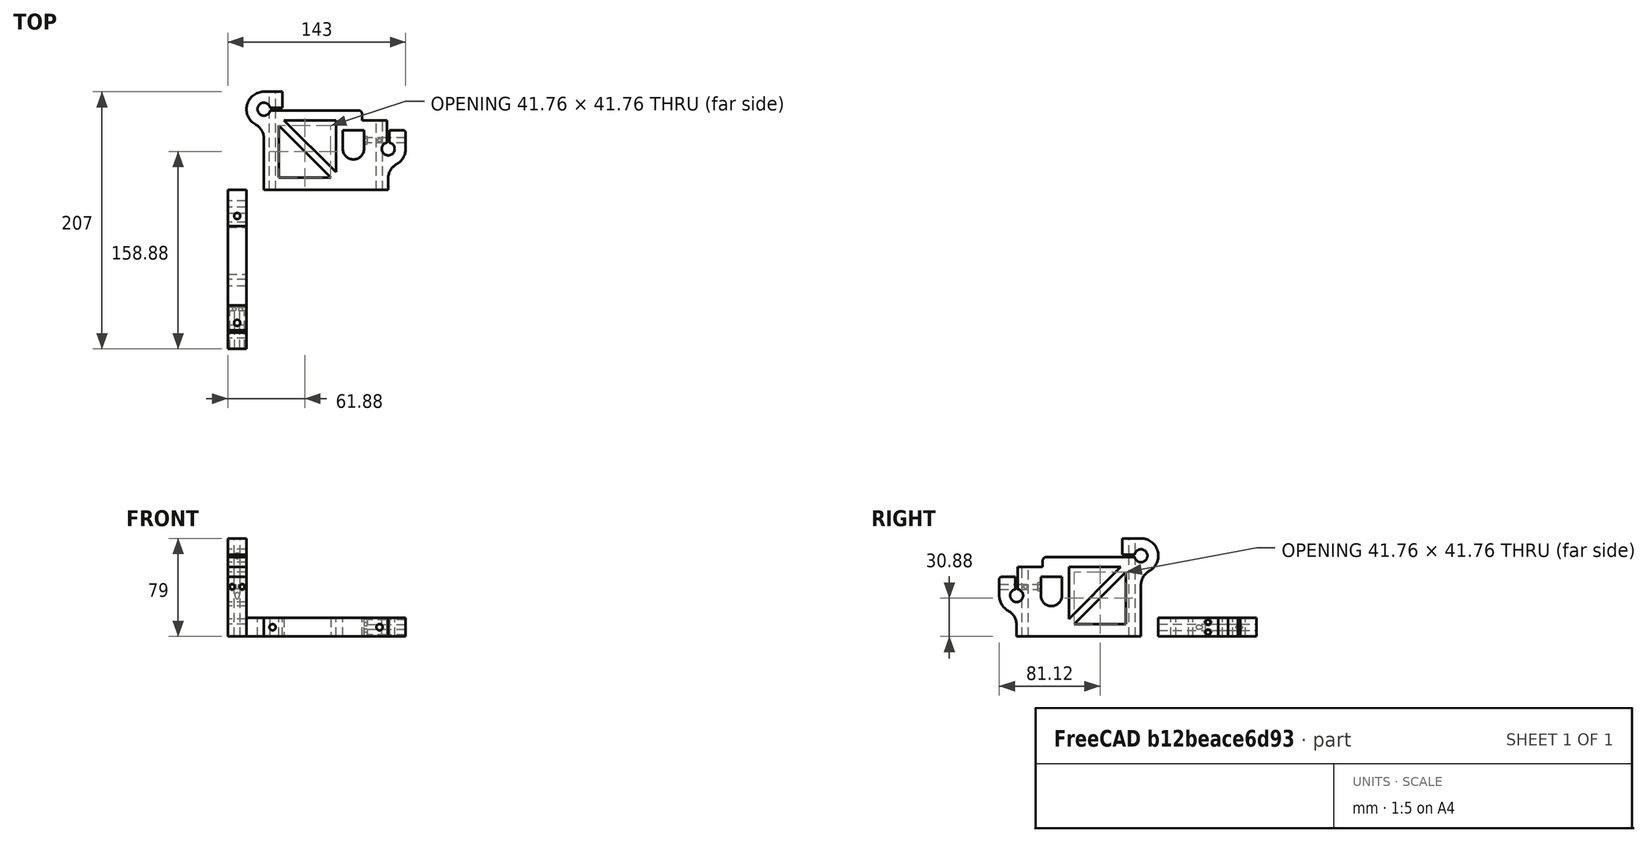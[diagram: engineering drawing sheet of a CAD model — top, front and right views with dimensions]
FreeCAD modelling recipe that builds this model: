
FCSTD DOCUMENT  (FreeCAD 0.15R4666 (Git))
Label: x_right_holder_A
License: All rights reserved
LicenseURL: http://en.wikipedia.org/wiki/All_rights_reserved
objects: Part::Box×9, Part::Cylinder×9, Part::MultiFuse×8, Part::Cut×7, Part::Fillet×3, Part::Prism×2, Part::Feature×2, Mesh::Feature×1
note: 40 computed .brp shape members not serialized (recipe doc carries the construction recipe); baked Part::Feature solids carry a one-line shape summary decoded from their .brp

FEATURE [Part::Box] Box  label="Cubo"
  Height = 15
  Length = 100
  Placement = pos=(14,0,0) rot=(0,0,1;0rad)
  Width = 56
FEATURE [Part::Box] Box001  label="Cubo001"
  Height = 15
  Length = 15
  Placement = pos=(14,56,0) rot=(0,0,1;0rad)
  Width = 23
FEATURE [Part::Box] Box002  label="Cubo002"
  Height = 15
  Length = 64
  Placement = pos=(29,56,0) rot=(0,0,1;0rad)
  Width = 8
FEATURE [Part::Box] Box003  label="Cubo003"
  Height = 15
  Length = 14
  Placement = pos=(114,33,0) rot=(0,0,1;0rad)
  Width = 15
FEATURE [Part::Cylinder] Cylinder  label="Cilindro"
  Angle = 360
  Height = 15
  Placement = pos=(14,65,0) rot=(0,0,1;0rad)
  Radius = 14
FEATURE [Part::Cylinder] Cylinder001  label="Cilindro001"
  Angle = 360
  Height = 15
  Placement = pos=(114,33,0) rot=(0,0,1;0rad)
  Radius = 14
FEATURE [Part::MultiFuse] Fusion
  Shapes = -> [Box,Cylinder001,Cylinder,Box003,Box002,Box001]
FEATURE [Part::Box] Box004  label="Cubo004"
  Height = 15
  Length = 46
  Placement = pos=(26,10,0) rot=(0,0,1;0rad)
  Width = 46
FEATURE [Part::Cut] Cut
  Base = -> Fusion
  Tool = -> Box004
FEATURE [Part::Fillet] Fillet
  Base = -> Cut
  Edges = 2 edges r=13: [Edge60,Edge63]
FEATURE [Part::Fillet] Fillet001
  Base = -> Fillet
  Edges = 1 edges r=3: [Edge76]
FEATURE [Part::Fillet] Fillet002  label="body"
  Base = -> Fillet001
  Edges = 1 edges r=2: [Edge89]
FEATURE [Part::Cylinder] Cylinder002  label="Cilindro002"
  Angle = 360
  Height = 17
  Placement = pos=(14,65,-1) rot=(0,0,1;0rad)
  Radius = 5.2
FEATURE [Part::Cylinder] Cylinder003  label="Cilindro003"
  Angle = 360
  Height = 17
  Placement = pos=(114,33,-1) rot=(0,0,1;0rad)
  Radius = 5.2
FEATURE [Part::MultiFuse] Fusion001  label="rod_holes"
  Shapes = -> [Cylinder002,Cylinder003]
FEATURE [Part::Box] Box006  label="Cubo006"
  Height = 15
  Length = 17
  Placement = pos=(77.5,33,0) rot=(0,0,1;0rad)
  Width = 15
FEATURE [Part::Cylinder] Cylinder004  label="Cilindro004"
  Angle = 360
  Height = 15
  Placement = pos=(86,33,0) rot=(0,0,1;0rad)
  Radius = 8.5
FEATURE [Part::MultiFuse] Fusion002  label="threaded_rod_hole"
  Shapes = -> [Box006,Cylinder004]
FEATURE [Part::Box] Box007  label="Cubo007"
  Height = 17
  Length = 12
  Placement = pos=(18,64,-1) rot=(0,0,1;0rad)
  Width = 2
FEATURE [Part::Box] Box008  label="Cubo008"
  Height = 17
  Length = 2
  Placement = pos=(113,37,-1) rot=(0,0,1;0rad)
  Width = 20
FEATURE [Part::MultiFuse] Fusion003  label="offset_holes"
  Shapes = -> [Box007,Box008]
FEATURE [Part::Cylinder] Cylinder005  label="Cilindro005"
  Angle = 360
  Height = 81
  Placement = pos=(21,-1,7.5) rot=(-1,0,0;1.5708rad)
  Radius = 2.5
FEATURE [Part::Cylinder] Cylinder006  label="Cilindro006"
  Angle = 360
  Height = 58
  Placement = pos=(107,-1,7.5) rot=(-1,0,0;1.5708rad)
  Radius = 2.5
FEATURE [Part::MultiFuse] Fusion004  label="vertical_holes"
  Shapes = -> [Cylinder005,Cylinder006]
FEATURE [Part::Cylinder] Cylinder007  label="Cilindro007"
  Angle = 360
  Height = 35
  Placement = pos=(129,40,3.5) rot=(0,-1,0;1.5708rad)
  Radius = 2
FEATURE [Part::Cylinder] Cylinder008  label="Cilindro008"
  Angle = 360
  Height = 35
  Placement = pos=(129,40,11.5) rot=(0,-1,0;1.5708rad)
  Radius = 2
FEATURE [Part::MultiFuse] Fusion005  label="screw_holes"
  Shapes = -> [Cylinder007,Cylinder008]
FEATURE [Part::Prism] Prism  label="Prisma"
  Circumradius = 3.2
  Height = 3
  Placement = pos=(94,40,3.5) rot=(0.250563,0.935113,0.250563;1.63783rad)
  Polygon = 6
FEATURE [Part::Prism] Prism001  label="Prisma001"
  Circumradius = 3.2
  Height = 3
  Placement = pos=(94,40,11.5) rot=(0.250563,0.935113,0.250563;1.63783rad)
  Polygon = 6
FEATURE [Part::MultiFuse] Fusion006  label="nut_holes"
  Shapes = -> [Prism,Prism001]
FEATURE [Part::Box] Box009  label="Cubo009"
  Height = 15
  Length = 66
  Placement = pos=(23.76,54,0) rot=(0,0,-1;0.785398rad)
  Width = 6
FEATURE [Part::Cut] Cut001
  Base = -> Fillet002
  Tool = -> Fusion002
FEATURE [Part::Cut] Cut002
  Base = -> Cut001
  Tool = -> Fusion006
FEATURE [Part::Cut] Cut003
  Base = -> Cut002
  Tool = -> Fusion003
FEATURE [Part::Cut] Cut004
  Base = -> Cut003
  Tool = -> Fusion001
FEATURE [Part::Cut] Cut005
  Base = -> Cut004
  Tool = -> Fusion004
FEATURE [Part::Cut] Cut006
  Base = -> Cut005
  Tool = -> Fusion005
FEATURE [Mesh::Feature] XholderRightinside002  label="XholderRightinside"
FEATURE [Part::Feature] XholderRightinside002001001  label="XholderRightinside002"
  shape: bbox 128 x 79.02 x 15 mm, 1393 faces, 0 solids (baked)
FEATURE [Part::MultiFuse] Fusion007  label="x_right_holder_A"
  Shapes = -> [Cut006,Box009]
FEATURE [Part::Feature] Fusion007_solid  label="x_right_holder_A (Solid)"
  Placement = pos=(0,0,0) rot=(0.57735,-0.57735,-0.57735;2.0944rad)
  shape: bbox 15 x 128 x 79 mm, 54 faces (baked)
